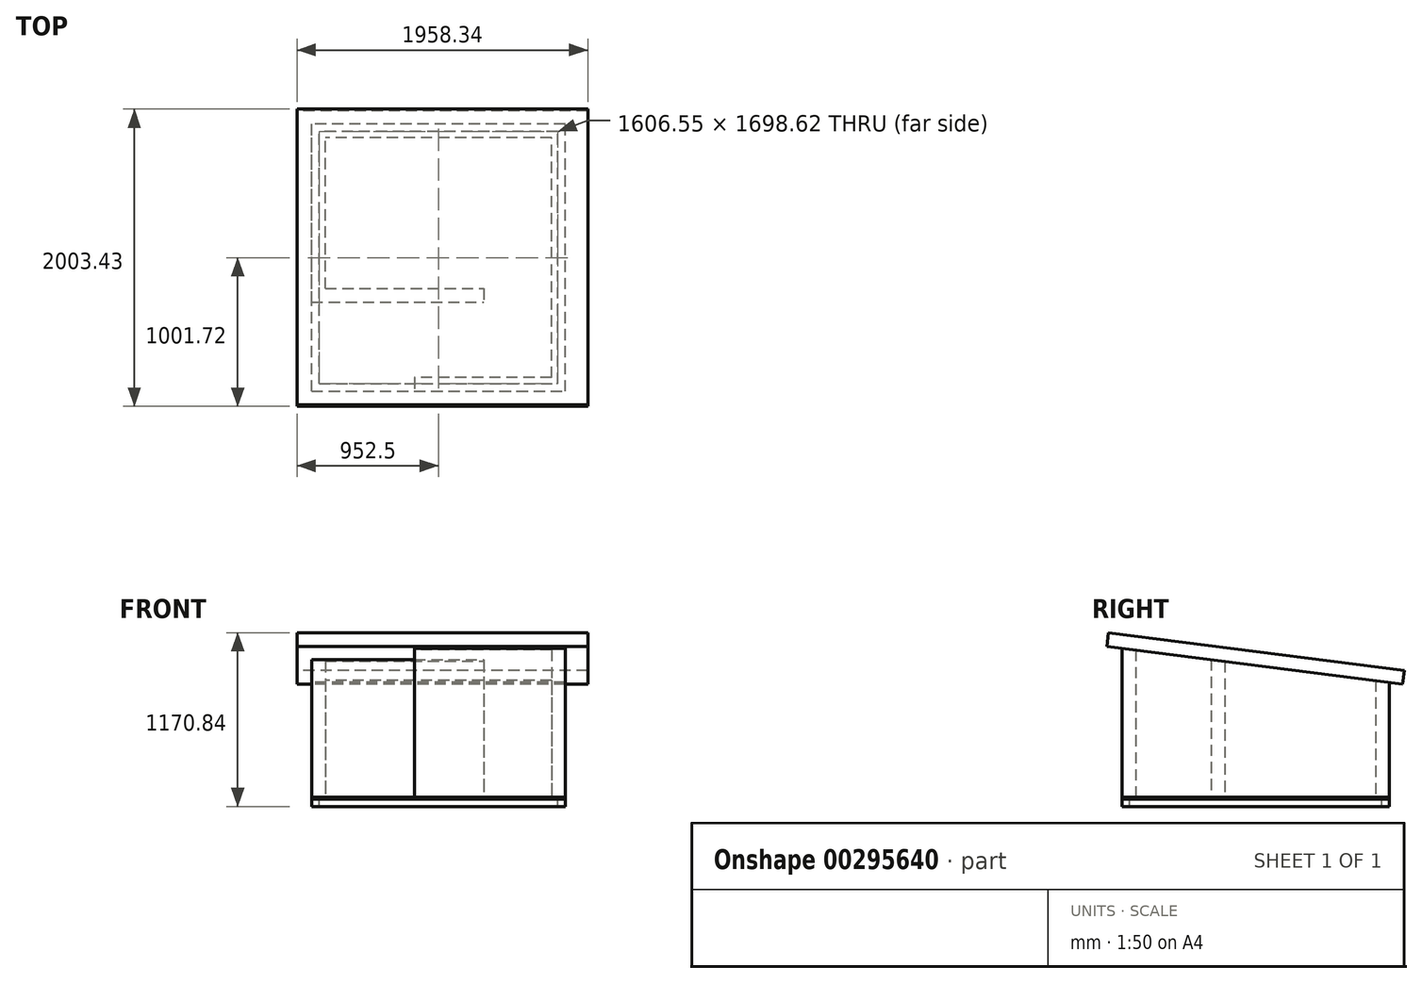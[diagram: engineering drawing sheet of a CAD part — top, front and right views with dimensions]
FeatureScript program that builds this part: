
annotation { "Feature Type Name" : "Feature", "Feature Type Description" : "" }
export const myFeature = defineFeature(function(context is Context, id is Id, definition is map)
    precondition{}
    {
        {
            var Q0;
            Q0=qCreatedBy(makeId("Top.planeOp"),FACE);
            var sketch = newSketch(context, id + "F0", { "sketchPlane" : qUnion([Q0])});
            skLineSegment(sketch, "E0.top", {"start": v(549.28, 1200.15) * mm, "end": v(-1158.87, 1200.15) * mm});
            skLineSegment(sketch, "E0.left", {"start": v(549.27, -600.08) * mm, "end": v(549.28, 1200.15) * mm});
            skLineSegment(sketch, "E0.right", {"start": v(-1158.88, 0) * mm, "end": v(-1158.87, 1200.15) * mm});
            skPoint(sketch, "E0.middle", {"position": v(0, 0) * mm});
            skLineSegment(sketch, "E1", {"start": v(-1158.88, 0) * mm, "end": v(0, 0) * mm});
            skLineSegment(sketch, "E2.0", {"start": v(-1066.8, 92.08) * mm, "end": v(0, 92.08) * mm});
            skLineSegment(sketch, "E2.2", {"start": v(457.2, -508) * mm, "end": v(457.2, 1108.07) * mm});
            skLineSegment(sketch, "E2.3", {"start": v(457.2, 1108.07) * mm, "end": v(-1066.8, 1108.08) * mm});
            skLineSegment(sketch, "E2.4", {"start": v(-1066.8, 92.07) * mm, "end": v(-1066.8, 1108.08) * mm});
            skLineSegment(sketch, "E3", {"start": v(0, 92.08) * mm, "end": v(0, 0) * mm});
            skLineSegment(sketch, "E4", {"start": v(-466.73, -600.08) * mm, "end": v(549.27, -600.08) * mm});
            skLineSegment(sketch, "E5", {"start": v(457.2, -508) * mm, "end": v(-466.73, -508) * mm});
            skLineSegment(sketch, "E6.trimOffspring", {"start": v(-466.73, -508) * mm, "end": v(-466.73, -600.08) * mm});
            skSolve(sketch);
        }
        {
            var Q0;
            Q0=qCreatedBy(makeId("Right.planeOp"),FACE);
            var sketch = newSketch(context, id + "F1", { "sketchPlane" : qUnion([Q0])});
            skLineSegment(sketch, "E7", {"start": v(-701.68, 1016) * mm, "end": v(1290.1, 762) * mm});
            skLineSegment(sketch, "E8", {"start": v(-701.68, 1016) * mm, "end": v(-690.03, 1107.34) * mm});
            skLineSegment(sketch, "E9", {"start": v(-690.03, 1107.34) * mm, "end": v(1301.75, 853.34) * mm});
            skLineSegment(sketch, "E10", {"start": v(1290.1, 762) * mm, "end": v(1301.75, 853.34) * mm});
            skSolve(sketch);
        }
        {
            var Q0;
            Q0=makeQuery(id+"F1.imprint","IMPRINT",FACE,{"disambiguationData":[TD([[makeQuery(id+"F1.imprint","IMPRINT",EDGE,{"derivedFrom":sQuery(id+"F1.wireOp",EDGE,"E7")}),1.0]])]});
            extrude(context, id + "F2", {"entities" : qUnion([Q0]), "depth" : 701.04 * mm, "hasSecondDirection" : true, "secondDirectionOppositeDirection" : true, "secondDirectionDepth" : 1257.3 * mm});
        }
        {
            var Q0;
            Q0 = qSketchRegion(id + "F0", true);
            var Q1;
            Q1=makeQuery(id+"F2.opExtrude","SWEPT_FACE",FACE,{"disambiguationData":[OSD([sQuery(id+"F1.wireOp",EDGE,"E7")])]});
            var Q2;
            Q2=makeQuery(id+"F2.opExtrude","SWEPT_BODY",BODY,{"disambiguationData":[OSD([sQuery(id+"F1.wireOp",EDGE,"E7"),sQuery(id+"F1.wireOp",EDGE,"E8"),sQuery(id+"F1.wireOp",EDGE,"E9"),sQuery(id+"F1.wireOp",EDGE,"E10")])]});
            extrude(context, id + "F3", {"entities" : qUnion([Q0]), "endBound" : BoundingType.UP_TO_SURFACE, "endBoundEntityFace" : qUnion([Q1]), "endBoundEntityBody" : qUnion([Q2]), "depth" : 25.4 * mm});
        }
        {
            var Q0;
            Q0=makeQuery(id+"F3.opExtrude","CAP_FACE",FACE,{"disambiguationData":[OSD([sQuery(id+"F0.wireOp",EDGE,"E0.top"),sQuery(id+"F0.wireOp",EDGE,"E0.left"),sQuery(id+"F0.wireOp",EDGE,"E0.right"),sQuery(id+"F0.wireOp",EDGE,"E1"),sQuery(id+"F0.wireOp",EDGE,"E2.0"),sQuery(id+"F0.wireOp",EDGE,"E2.2"),sQuery(id+"F0.wireOp",EDGE,"E2.3"),sQuery(id+"F0.wireOp",EDGE,"E2.4"),sQuery(id+"F0.wireOp",EDGE,"E3"),sQuery(id+"F0.wireOp",EDGE,"E4"),sQuery(id+"F0.wireOp",EDGE,"E5"),sQuery(id+"F0.wireOp",EDGE,"E6.trimOffspring")])],"isStart":true});
            var sketch = newSketch(context, id + "F4", { "sketchPlane" : qUnion([Q0])});
            skLineSegment(sketch, "E11", {"start": v(-1158.87, -1200.15) * mm, "end": v(549.28, -1200.15) * mm});
            skLineSegment(sketch, "E12", {"start": v(549.28, -1200.15) * mm, "end": v(549.28, 600.08) * mm});
            skLineSegment(sketch, "E13", {"start": v(549.27, 600.08) * mm, "end": v(-1158.88, 600.07) * mm});
            skPoint(sketch, "E13.endSnap0", {"position": v(-1158.87, -600.08) * mm});
            skLineSegment(sketch, "E14", {"start": v(-1158.88, 600.07) * mm, "end": v(-1158.87, -1200.15) * mm});
            skSolve(sketch);
        }
        {
            var Q0;
            Q0 = qSketchRegion(id + "F4", true);
            extrude(context, id + "F5", {"entities" : qUnion([Q0]), "depth" : 12.7 * mm});
        }
        {
            var Q0;
            Q0=makeQuery(id+"F5.opExtrude","CAP_FACE",FACE,{"disambiguationData":[OSD([sQuery(id+"F4.wireOp",EDGE,"E11"),sQuery(id+"F4.wireOp",EDGE,"E12"),sQuery(id+"F4.wireOp",EDGE,"E13"),sQuery(id+"F4.wireOp",EDGE,"E14")])],"isStart":false});
            var sketch = newSketch(context, id + "F6", { "sketchPlane" : qUnion([Q0])});
            skLineSegment(sketch, "E15.0", {"start": v(-1158.88, 600.07) * mm, "end": v(-1158.87, -1200.15) * mm});
            skLineSegment(sketch, "E16.0", {"start": v(-1158.88, 600.08) * mm, "end": v(549.27, 600.08) * mm});
            skLineSegment(sketch, "E17.0", {"start": v(549.27, 600.08) * mm, "end": v(549.28, -1200.15) * mm});
            skLineSegment(sketch, "E18.0", {"start": v(-1108.08, 549.28) * mm, "end": v(-1108.07, -1149.35) * mm});
            skLineSegment(sketch, "E18.1", {"start": v(-1108.08, 549.28) * mm, "end": v(498.47, 549.28) * mm});
            skLineSegment(sketch, "E18.2", {"start": v(498.47, 549.28) * mm, "end": v(498.48, -1149.35) * mm});
            skLineSegment(sketch, "E18.3", {"start": v(498.48, -1149.35) * mm, "end": v(-1108.07, -1149.35) * mm});
            skSolve(sketch);
        }
        {
            var Q0;
            Q0=makeQuery(id+"F6.imprint","IMPRINT",FACE,{"disambiguationData":[TD([[makeQuery(id+"F6.imprint","IMPRINT",EDGE,{"derivedFrom":sQuery(id+"F6.wireOp",EDGE,"E15.0")}),1.0]])]});
            extrude(context, id + "F7", {"entities" : qUnion([Q0]), "depth" : 50.8 * mm});
        }
    });
